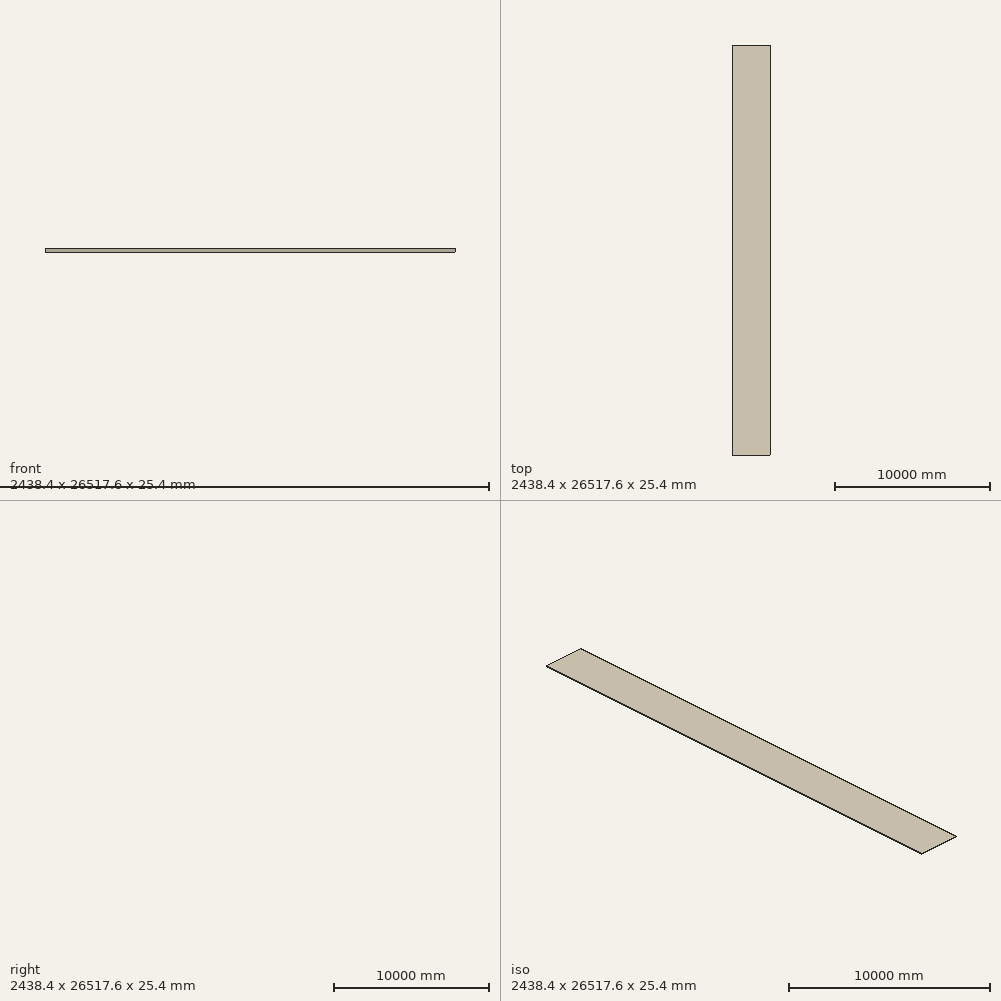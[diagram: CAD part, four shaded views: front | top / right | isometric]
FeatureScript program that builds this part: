
annotation { "Feature Type Name" : "Feature", "Feature Type Description" : "" }
export const myFeature = defineFeature(function(context is Context, id is Id, definition is map)
    precondition{}
    {
        {
            var Q0;
            Q0=qCreatedBy(makeId("Top.planeOp"),FACE);
            var sketch = newSketch(context, id + "F0", { "sketchPlane" : qUnion([Q0])});
            skLineSegment(sketch, "E0.bottom", {"start": v(-1219.2, -13258.8) * mm, "end": v(1219.2, -13258.8) * mm});
            skLineSegment(sketch, "E0.top", {"start": v(-1219.2, 13258.8) * mm, "end": v(1219.2, 13258.8) * mm});
            skLineSegment(sketch, "E0.left", {"start": v(-1219.2, -13258.8) * mm, "end": v(-1219.2, 13258.8) * mm});
            skLineSegment(sketch, "E0.right", {"start": v(1219.2, -13258.8) * mm, "end": v(1219.2, 13258.8) * mm});
            skPoint(sketch, "E0.middle", {"position": v(0, 0) * mm});
            skSolve(sketch);
        }
        {
            var Q0;
            Q0 = qSketchRegion(id + "F0", true);
            extrude(context, id + "F1", {"entities" : qUnion([Q0]), "depth" : 25.4 * mm, "offsetDistance" : 25.4 * mm});
        }
    });
